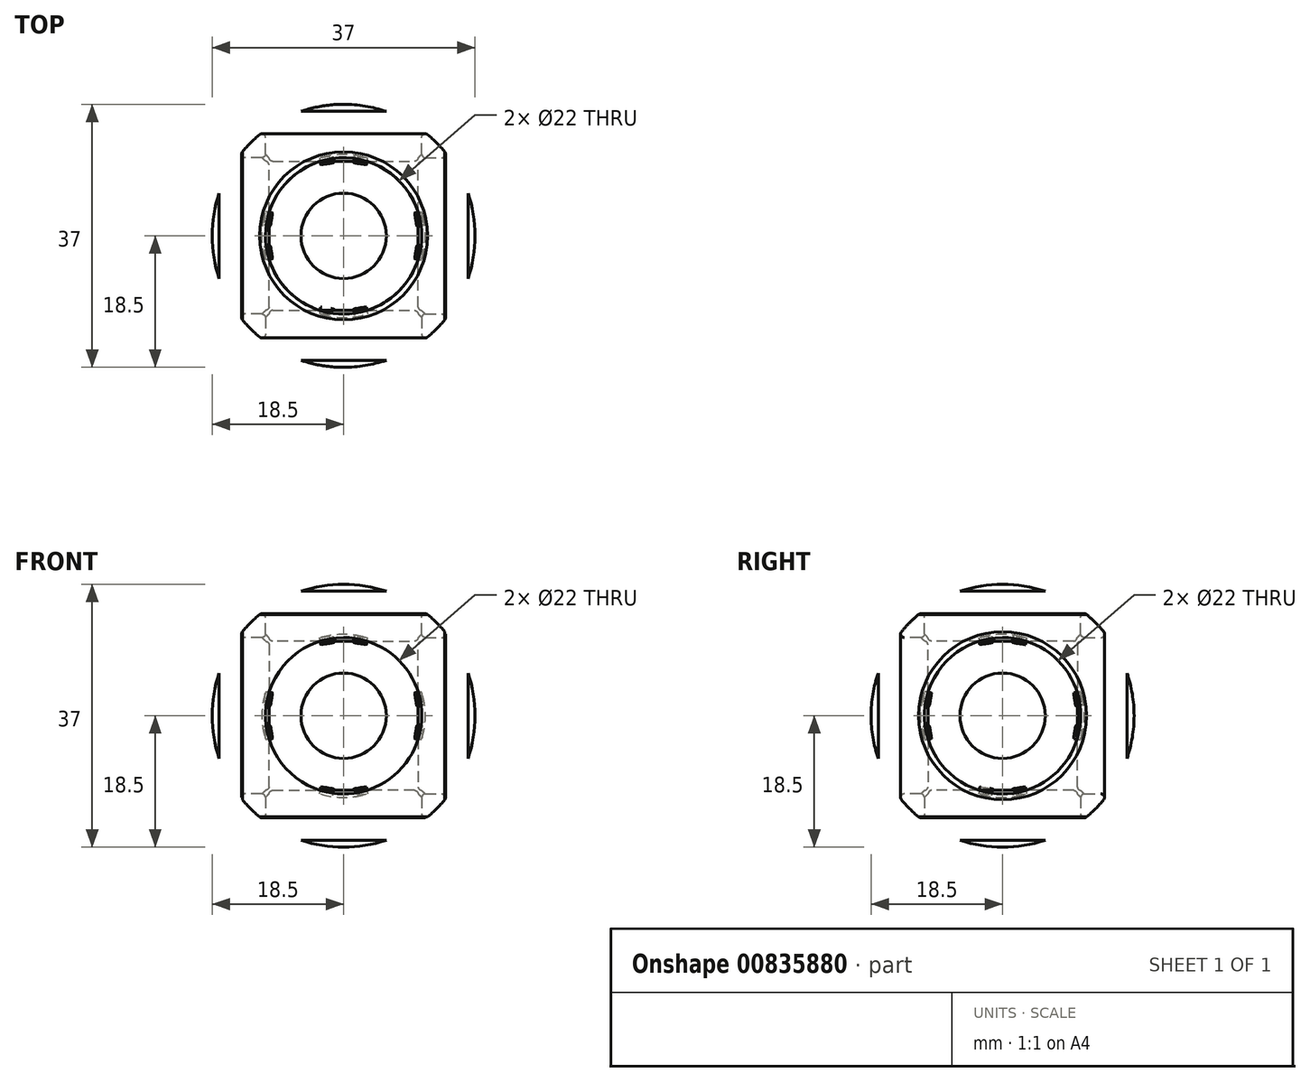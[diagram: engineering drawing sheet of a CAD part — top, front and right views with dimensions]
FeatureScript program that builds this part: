
annotation { "Feature Type Name" : "Feature", "Feature Type Description" : "" }
export const myFeature = defineFeature(function(context is Context, id is Id, definition is map)
    precondition{}
    {
        {
            var Q0;
            Q0=qCreatedBy(makeId("Top.planeOp"),FACE);
            var sketch = newSketch(context, id + "F0", { "sketchPlane" : qUnion([Q0])});
            skCircle(sketch, "E0", {"center": v(0, 0) * mm, "radius": 18.5 * mm});
            skLineSegment(sketch, "E1", {"start": v(0, 18.5) * mm, "end": v(0, -18.5) * mm});
            skSolve(sketch);
        }
        {
            var Q0;
            {var subQ0=sQuery(id+"F0.wireOp",EDGE,"E1");Q0=makeQuery(id+"F0.imprint","IMPRINT",FACE,{"disambiguationData":[TD([[makeQuery(id+"F0.imprint","IMPRINT",EDGE,{"derivedFrom":subQ0}),1.0]])]});}
            var Q1;
            Q1=sQuery(id+"F0.wireOp",EDGE,"E1");
            revolve(context, id + "F1", {"surfaceOperationType" : NewSurfaceOperationType.NEW, "entities" : qUnion([Q0]), "axis" : qUnion([Q1]), "revolveType" : RevolveType.FULL});
        }
        {
            var Q0;
            Q0=qCreatedBy(makeId("Right.planeOp"),FACE);
            cPlane(context, id + "F2", {"entities" : qUnion([Q0]), "cplaneType" : CPlaneType.OFFSET, "offset" : 17.5 * mm, "width" : 150 * mm, "height" : 150 * mm});
        }
        {
            var Q0;
            Q0=qCreatedBy(id+"F2.planeOp",FACE);
            var sketch = newSketch(context, id + "F3", { "sketchPlane" : qUnion([Q0])});
            skCircle(sketch, "E2", {"center": v(0, 0) * mm, "radius": 11 * mm});
            skSolve(sketch);
        }
        {
            var Q0;
            Q0 = qSketchRegion(id + "F3", true);
            extrude(context, id + "F4", {"entities" : qUnion([Q0]), "operationType" : NewBodyOperationType.REMOVE, "oppositeDirection" : true, "depth" : 7 * mm, "offsetDistance" : 25 * mm});
        }
        {
            var Q0;
            Q0=qCreatedBy(makeId("Front.planeOp"),FACE);
            cPlane(context, id + "F5", {"entities" : qUnion([Q0]), "cplaneType" : CPlaneType.OFFSET, "offset" : 17.5 * mm, "width" : 150 * mm, "height" : 150 * mm});
        }
        {
            var Q0;
            Q0=qCreatedBy(id+"F5.planeOp",FACE);
            var sketch = newSketch(context, id + "F6", { "sketchPlane" : qUnion([Q0])});
            skCircle(sketch, "E3", {"center": v(0, 0) * mm, "radius": 11 * mm});
            skSolve(sketch);
        }
        {
            var Q0;
            Q0 = qSketchRegion(id + "F6", true);
            extrude(context, id + "F7", {"entities" : qUnion([Q0]), "operationType" : NewBodyOperationType.REMOVE, "oppositeDirection" : true, "depth" : 7 * mm, "offsetDistance" : 25 * mm});
        }
        {
            var Q0;
            Q0=qCreatedBy(makeId("Front.planeOp"),FACE);
            cPlane(context, id + "F8", {"entities" : qUnion([Q0]), "cplaneType" : CPlaneType.OFFSET, "offset" : 17.5 * mm, "oppositeDirection" : true, "width" : 150 * mm, "height" : 150 * mm});
        }
        {
            var Q0;
            Q0=qCreatedBy(id+"F8.planeOp",FACE);
            var sketch = newSketch(context, id + "F9", { "sketchPlane" : qUnion([Q0])});
            skCircle(sketch, "E4", {"center": v(0, 0) * mm, "radius": 11 * mm});
            skSolve(sketch);
        }
        {
            var Q0;
            Q0 = qSketchRegion(id + "F9", true);
            extrude(context, id + "F10", {"entities" : qUnion([Q0]), "operationType" : NewBodyOperationType.REMOVE, "depth" : 7 * mm, "offsetDistance" : 25 * mm});
        }
        {
            var Q0;
            Q0=qCreatedBy(makeId("Right.planeOp"),FACE);
            cPlane(context, id + "F11", {"entities" : qUnion([Q0]), "cplaneType" : CPlaneType.OFFSET, "offset" : 17.5 * mm, "oppositeDirection" : true, "width" : 150 * mm, "height" : 150 * mm});
        }
        {
            var Q0;
            Q0=qCreatedBy(id+"F11.planeOp",FACE);
            var sketch = newSketch(context, id + "F12", { "sketchPlane" : qUnion([Q0])});
            skCircle(sketch, "E5", {"center": v(0, 0) * mm, "radius": 11 * mm});
            skSolve(sketch);
        }
        {
            var Q0;
            Q0 = qSketchRegion(id + "F12", true);
            extrude(context, id + "F13", {"entities" : qUnion([Q0]), "operationType" : NewBodyOperationType.REMOVE, "depth" : 7 * mm, "offsetDistance" : 25 * mm});
        }
        {
            var Q0;
            Q0=qCreatedBy(makeId("Top.planeOp"),FACE);
            cPlane(context, id + "F14", {"entities" : qUnion([Q0]), "cplaneType" : CPlaneType.OFFSET, "offset" : 17.5 * mm, "width" : 150 * mm, "height" : 150 * mm});
        }
        {
            var Q0;
            Q0=qCreatedBy(id+"F14.planeOp",FACE);
            var sketch = newSketch(context, id + "F15", { "sketchPlane" : qUnion([Q0])});
            skCircle(sketch, "E6", {"center": v(0, 0) * mm, "radius": 11 * mm});
            skSolve(sketch);
        }
        {
            var Q0;
            Q0 = qSketchRegion(id + "F15", true);
            extrude(context, id + "F16", {"entities" : qUnion([Q0]), "operationType" : NewBodyOperationType.REMOVE, "oppositeDirection" : true, "depth" : 7 * mm, "offsetDistance" : 25 * mm});
        }
        {
            var Q0;
            Q0=qCreatedBy(makeId("Top.planeOp"),FACE);
            cPlane(context, id + "F17", {"entities" : qUnion([Q0]), "cplaneType" : CPlaneType.OFFSET, "offset" : 17.5 * mm, "oppositeDirection" : true, "width" : 150 * mm, "height" : 150 * mm});
        }
        {
            var Q0;
            Q0=qCreatedBy(id+"F17.planeOp",FACE);
            var sketch = newSketch(context, id + "F18", { "sketchPlane" : qUnion([Q0])});
            skCircle(sketch, "E7", {"center": v(0, 0) * mm, "radius": 11 * mm});
            skSolve(sketch);
        }
        {
            var Q0;
            Q0 = qSketchRegion(id + "F18", true);
            extrude(context, id + "F19", {"entities" : qUnion([Q0]), "operationType" : NewBodyOperationType.REMOVE, "depth" : 7 * mm, "offsetDistance" : 25 * mm});
        }
        {
            var Q0;
            Q0=makeQuery(id+"F16.boolean.opBoolean","COPY",FACE,{"derivedFrom":makeQuery(id+"F16.opExtrude","SWEPT_FACE",FACE,{"disambiguationData":[OSD([sQuery(id+"F15.wireOp",EDGE,"E6")])]})});
            var Q1;
            Q1=makeQuery(id+"F16.boolean.opBoolean","INTERSECT",EDGE,{"derivedFrom":[makeQuery(id+"F1.opRevolve","SWEPT_FACE",FACE,{"disambiguationData":[OSD([sQuery(id+"F0.wireOp",EDGE,"E0")])]}),makeQuery(id+"F16.opExtrude","SWEPT_FACE",FACE,{"disambiguationData":[OSD([sQuery(id+"F15.wireOp",EDGE,"E6")])]})]});
            var Q2;
            Q2=makeQuery(id+"F16.boolean.opBoolean","COPY",FACE,{"derivedFrom":makeQuery(id+"F16.opExtrude","CAP_FACE",FACE,{"disambiguationData":[OSD([sQuery(id+"F15.wireOp",EDGE,"E6")])],"isStart":false})});
            var Q3;
            Q3=makeQuery(id+"F16.boolean.opBoolean","INTERSECT",EDGE,{"derivedFrom":[makeQuery(id+"F10.boolean.opBoolean","COPY",FACE,{"derivedFrom":makeQuery(id+"F10.opExtrude","SWEPT_FACE",FACE,{"disambiguationData":[OSD([sQuery(id+"F9.wireOp",EDGE,"E4")])]})}),makeQuery(id+"F16.opExtrude","SWEPT_FACE",FACE,{"disambiguationData":[OSD([sQuery(id+"F15.wireOp",EDGE,"E6")])]})]});
            var Q4;
            Q4=makeQuery(id+"F13.boolean.opBoolean","COPY",FACE,{"derivedFrom":makeQuery(id+"F13.opExtrude","SWEPT_FACE",FACE,{"disambiguationData":[OSD([sQuery(id+"F12.wireOp",EDGE,"E5")])]})});
            var Q5;
            Q5=makeQuery(id+"F10.boolean.opBoolean","COPY",FACE,{"derivedFrom":makeQuery(id+"F10.opExtrude","SWEPT_FACE",FACE,{"disambiguationData":[OSD([sQuery(id+"F9.wireOp",EDGE,"E4")])]})});
            var Q6;
            Q6=makeQuery(id+"F1.opRevolve","SWEPT_FACE",FACE,{"disambiguationData":[OSD([sQuery(id+"F0.wireOp",EDGE,"E0")])]});
            var Q7;
            Q7=makeQuery(id+"F4.boolean.opBoolean","INTERSECT",EDGE,{"derivedFrom":[makeQuery(id+"F1.opRevolve","SWEPT_FACE",FACE,{"disambiguationData":[OSD([sQuery(id+"F0.wireOp",EDGE,"E0")])]}),makeQuery(id+"F4.opExtrude","SWEPT_FACE",FACE,{"disambiguationData":[OSD([sQuery(id+"F3.wireOp",EDGE,"E2")])]})]});
            var Q8;
            Q8=makeQuery(id+"F13.boolean.opBoolean","INTERSECT",EDGE,{"derivedFrom":[makeQuery(id+"F1.opRevolve","SWEPT_FACE",FACE,{"disambiguationData":[OSD([sQuery(id+"F0.wireOp",EDGE,"E0")])]}),makeQuery(id+"F13.opExtrude","SWEPT_FACE",FACE,{"disambiguationData":[OSD([sQuery(id+"F12.wireOp",EDGE,"E5")])]})]});
            var Q9;
            Q9=makeQuery(id+"F7.boolean.opBoolean","INTERSECT",EDGE,{"derivedFrom":[makeQuery(id+"F1.opRevolve","SWEPT_FACE",FACE,{"disambiguationData":[OSD([sQuery(id+"F0.wireOp",EDGE,"E0")])]}),makeQuery(id+"F7.opExtrude","SWEPT_FACE",FACE,{"disambiguationData":[OSD([sQuery(id+"F6.wireOp",EDGE,"E3")])]})]});
            var Q10;
            Q10=makeQuery(id+"F10.boolean.opBoolean","INTERSECT",EDGE,{"derivedFrom":[makeQuery(id+"F1.opRevolve","SWEPT_FACE",FACE,{"disambiguationData":[OSD([sQuery(id+"F0.wireOp",EDGE,"E0")])]}),makeQuery(id+"F10.opExtrude","SWEPT_FACE",FACE,{"disambiguationData":[OSD([sQuery(id+"F9.wireOp",EDGE,"E4")])]})]});
            var Q11;
            Q11=makeQuery(id+"F16.boolean.opBoolean","INTERSECT",EDGE,{"derivedFrom":[makeQuery(id+"F4.boolean.opBoolean","COPY",FACE,{"derivedFrom":makeQuery(id+"F4.opExtrude","SWEPT_FACE",FACE,{"disambiguationData":[OSD([sQuery(id+"F3.wireOp",EDGE,"E2")])]})}),makeQuery(id+"F16.opExtrude","SWEPT_FACE",FACE,{"disambiguationData":[OSD([sQuery(id+"F15.wireOp",EDGE,"E6")])]})]});
            var Q12;
            {var subQ0=sQuery(id+"F12.wireOp",EDGE,"E5");var subQ1=sQuery(id+"F6.wireOp",EDGE,"E3");Q12=makeQuery(id+"F16.boolean.opBoolean","SPLIT",EDGE,{"disambiguationData":[TD([makeQuery(id+"F7.boolean.opBoolean","COPY",FACE,{"derivedFrom":makeQuery(id+"F7.opExtrude","SWEPT_FACE",FACE,{"disambiguationData":[OSD([subQ1])]})})])],"derivedFrom":makeQuery(id+"F13.boolean.opBoolean","COPY",EDGE,{"disambiguationData":[OD(1.0)],"derivedFrom":makeQuery(id+"F13.opExtrude","CAP_EDGE",EDGE,{"disambiguationData":[OSD([subQ0])],"isStart":false})})});}
            var Q13;
            {var subQ0=sQuery(id+"F12.wireOp",EDGE,"E5");var subQ1=sQuery(id+"F9.wireOp",EDGE,"E4");Q13=makeQuery(id+"F16.boolean.opBoolean","SPLIT",EDGE,{"disambiguationData":[TD([makeQuery(id+"F13.boolean.opBoolean","COPY",FACE,{"derivedFrom":makeQuery(id+"F13.opExtrude","SWEPT_FACE",FACE,{"disambiguationData":[OSD([subQ0])]})})])],"derivedFrom":makeQuery(id+"F13.boolean.opBoolean","SPLIT",EDGE,{"disambiguationData":[OD(1.0)],"derivedFrom":makeQuery(id+"F10.boolean.opBoolean","COPY",EDGE,{"derivedFrom":makeQuery(id+"F10.opExtrude","CAP_EDGE",EDGE,{"disambiguationData":[OSD([subQ1])],"isStart":false})})})});}
            var Q14;
            {var subQ0=sQuery(id+"F9.wireOp",EDGE,"E4");var subQ1=sQuery(id+"F3.wireOp",EDGE,"E2");Q14=makeQuery(id+"F16.boolean.opBoolean","SPLIT",EDGE,{"disambiguationData":[TD([makeQuery(id+"F4.boolean.opBoolean","COPY",FACE,{"derivedFrom":makeQuery(id+"F4.opExtrude","SWEPT_FACE",FACE,{"disambiguationData":[OSD([subQ1])]})})])],"derivedFrom":makeQuery(id+"F13.boolean.opBoolean","SPLIT",EDGE,{"disambiguationData":[OD(1.0)],"derivedFrom":makeQuery(id+"F10.boolean.opBoolean","COPY",EDGE,{"derivedFrom":makeQuery(id+"F10.opExtrude","CAP_EDGE",EDGE,{"disambiguationData":[OSD([subQ0])],"isStart":false})})})});}
            var Q15;
            Q15=makeQuery(id+"F16.boolean.opBoolean","INTERSECT",EDGE,{"derivedFrom":[makeQuery(id+"F13.boolean.opBoolean","COPY",FACE,{"derivedFrom":makeQuery(id+"F13.opExtrude","SWEPT_FACE",FACE,{"disambiguationData":[OSD([sQuery(id+"F12.wireOp",EDGE,"E5")])]})}),makeQuery(id+"F16.opExtrude","SWEPT_FACE",FACE,{"disambiguationData":[OSD([sQuery(id+"F15.wireOp",EDGE,"E6")])]})]});
            var Q16;
            Q16=makeQuery(id+"F4.boolean.opBoolean","COPY",FACE,{"derivedFrom":makeQuery(id+"F4.opExtrude","SWEPT_FACE",FACE,{"disambiguationData":[OSD([sQuery(id+"F3.wireOp",EDGE,"E2")])]})});
            var Q17;
            Q17=makeQuery(id+"F16.boolean.opBoolean","INTERSECT",EDGE,{"derivedFrom":[makeQuery(id+"F7.boolean.opBoolean","COPY",FACE,{"derivedFrom":makeQuery(id+"F7.opExtrude","SWEPT_FACE",FACE,{"disambiguationData":[OSD([sQuery(id+"F6.wireOp",EDGE,"E3")])]})}),makeQuery(id+"F16.opExtrude","SWEPT_FACE",FACE,{"disambiguationData":[OSD([sQuery(id+"F15.wireOp",EDGE,"E6")])]})]});
            var Q18;
            Q18=makeQuery(id+"F19.boolean.opBoolean","COPY",FACE,{"derivedFrom":makeQuery(id+"F19.opExtrude","CAP_FACE",FACE,{"disambiguationData":[OSD([sQuery(id+"F18.wireOp",EDGE,"E7")])],"isStart":false})});
            var Q19;
            Q19=makeQuery(id+"F16.boolean.opBoolean","INTERSECT",EDGE,{"derivedFrom":[makeQuery(id+"F13.boolean.opBoolean","COPY",FACE,{"derivedFrom":makeQuery(id+"F13.opExtrude","CAP_FACE",FACE,{"disambiguationData":[OSD([sQuery(id+"F12.wireOp",EDGE,"E5")])],"isStart":false})}),makeQuery(id+"F16.opExtrude","CAP_FACE",FACE,{"disambiguationData":[OSD([sQuery(id+"F15.wireOp",EDGE,"E6")])],"isStart":false})]});
            var Q20;
            Q20=makeQuery(id+"F16.boolean.opBoolean","INTERSECT",EDGE,{"derivedFrom":[makeQuery(id+"F10.boolean.opBoolean","COPY",FACE,{"derivedFrom":makeQuery(id+"F10.opExtrude","CAP_FACE",FACE,{"disambiguationData":[OSD([sQuery(id+"F9.wireOp",EDGE,"E4")])],"isStart":false})}),makeQuery(id+"F16.opExtrude","CAP_FACE",FACE,{"disambiguationData":[OSD([sQuery(id+"F15.wireOp",EDGE,"E6")])],"isStart":false})]});
            var Q21;
            {var subQ0=sQuery(id+"F6.wireOp",EDGE,"E3");var subQ2=sQuery(id+"F3.wireOp",EDGE,"E2");Q21=makeQuery(id+"F16.boolean.opBoolean","SPLIT",EDGE,{"disambiguationData":[TD([makeQuery(id+"F7.boolean.opBoolean","COPY",FACE,{"derivedFrom":makeQuery(id+"F7.opExtrude","SWEPT_FACE",FACE,{"disambiguationData":[OSD([subQ0])]})})])],"derivedFrom":makeQuery(id+"F10.boolean.opBoolean","SPLIT",EDGE,{"disambiguationData":[OD(1.0)],"derivedFrom":makeQuery(id+"F4.boolean.opBoolean","COPY",EDGE,{"derivedFrom":makeQuery(id+"F4.opExtrude","CAP_EDGE",EDGE,{"disambiguationData":[OSD([subQ2])],"isStart":false})})})});}
            var Q22;
            {var subQ0=sQuery(id+"F9.wireOp",EDGE,"E4");var subQ1=sQuery(id+"F3.wireOp",EDGE,"E2");Q22=makeQuery(id+"F16.boolean.opBoolean","SPLIT",EDGE,{"disambiguationData":[TD([makeQuery(id+"F10.boolean.opBoolean","COPY",FACE,{"derivedFrom":makeQuery(id+"F10.opExtrude","SWEPT_FACE",FACE,{"disambiguationData":[OSD([subQ0])]})})])],"derivedFrom":makeQuery(id+"F10.boolean.opBoolean","SPLIT",EDGE,{"disambiguationData":[OD(1.0)],"derivedFrom":makeQuery(id+"F4.boolean.opBoolean","COPY",EDGE,{"derivedFrom":makeQuery(id+"F4.opExtrude","CAP_EDGE",EDGE,{"disambiguationData":[OSD([subQ1])],"isStart":false})})})});}
            var Q23;
            {var subQ0=sQuery(id+"F6.wireOp",EDGE,"E3");var subQ2=sQuery(id+"F3.wireOp",EDGE,"E2");Q23=makeQuery(id+"F16.boolean.opBoolean","SPLIT",EDGE,{"disambiguationData":[TD([makeQuery(id+"F4.boolean.opBoolean","COPY",FACE,{"derivedFrom":makeQuery(id+"F4.opExtrude","SWEPT_FACE",FACE,{"disambiguationData":[OSD([subQ2])]})})])],"derivedFrom":makeQuery(id+"F13.boolean.opBoolean","SPLIT",EDGE,{"disambiguationData":[OD(1.0)],"derivedFrom":makeQuery(id+"F7.boolean.opBoolean","COPY",EDGE,{"derivedFrom":makeQuery(id+"F7.opExtrude","CAP_EDGE",EDGE,{"disambiguationData":[OSD([subQ0])],"isStart":false})})})});}
            var Q24;
            {var subQ0=sQuery(id+"F12.wireOp",EDGE,"E5");var subQ1=sQuery(id+"F6.wireOp",EDGE,"E3");Q24=makeQuery(id+"F16.boolean.opBoolean","SPLIT",EDGE,{"disambiguationData":[TD([makeQuery(id+"F13.boolean.opBoolean","COPY",FACE,{"derivedFrom":makeQuery(id+"F13.opExtrude","SWEPT_FACE",FACE,{"disambiguationData":[OSD([subQ0])]})})])],"derivedFrom":makeQuery(id+"F13.boolean.opBoolean","SPLIT",EDGE,{"disambiguationData":[OD(1.0)],"derivedFrom":makeQuery(id+"F7.boolean.opBoolean","COPY",EDGE,{"derivedFrom":makeQuery(id+"F7.opExtrude","CAP_EDGE",EDGE,{"disambiguationData":[OSD([subQ1])],"isStart":false})})})});}
            var Q25;
            {var subQ0=sQuery(id+"F12.wireOp",EDGE,"E5");var subQ1=sQuery(id+"F9.wireOp",EDGE,"E4");Q25=makeQuery(id+"F16.boolean.opBoolean","SPLIT",EDGE,{"disambiguationData":[TD([makeQuery(id+"F10.boolean.opBoolean","COPY",FACE,{"derivedFrom":makeQuery(id+"F10.opExtrude","SWEPT_FACE",FACE,{"disambiguationData":[OSD([subQ1])]})})])],"derivedFrom":makeQuery(id+"F13.boolean.opBoolean","COPY",EDGE,{"disambiguationData":[OD(1.0)],"derivedFrom":makeQuery(id+"F13.opExtrude","CAP_EDGE",EDGE,{"disambiguationData":[OSD([subQ0])],"isStart":false})})});}
            var Q26;
            {var subQ0=sQuery(id+"F6.wireOp",EDGE,"E3");var subQ1=sQuery(id+"F15.wireOp",EDGE,"E6");var subQ2=sQuery(id+"F3.wireOp",EDGE,"E2");Q26=makeQuery(id+"F16.boolean.opBoolean","COPY",EDGE,{"disambiguationData":[TD([makeQuery(id+"F4.boolean.opBoolean","COPY",FACE,{"derivedFrom":makeQuery(id+"F4.opExtrude","SWEPT_FACE",FACE,{"disambiguationData":[OSD([subQ2])]})}),makeQuery(id+"F4.boolean.opBoolean","COPY",FACE,{"derivedFrom":makeQuery(id+"F4.opExtrude","CAP_FACE",FACE,{"disambiguationData":[OSD([subQ2])],"isStart":false})}),makeQuery(id+"F7.boolean.opBoolean","COPY",FACE,{"derivedFrom":makeQuery(id+"F7.opExtrude","SWEPT_FACE",FACE,{"disambiguationData":[OSD([subQ0])]})}),makeQuery(id+"F7.boolean.opBoolean","COPY",FACE,{"derivedFrom":makeQuery(id+"F7.opExtrude","CAP_FACE",FACE,{"disambiguationData":[OSD([subQ0])],"isStart":false})}),makeQuery(id+"F16.opExtrude","SWEPT_FACE",FACE,{"disambiguationData":[OSD([subQ1])]}),makeQuery(id+"F16.opExtrude","CAP_FACE",FACE,{"disambiguationData":[OSD([subQ1])],"isStart":false})])],"derivedFrom":makeQuery(id+"F16.opExtrude","CAP_EDGE",EDGE,{"disambiguationData":[OSD([subQ1])],"isStart":false})});}
            var Q27;
            {var subQ0=sQuery(id+"F9.wireOp",EDGE,"E4");var subQ1=sQuery(id+"F3.wireOp",EDGE,"E2");var subQ2=sQuery(id+"F15.wireOp",EDGE,"E6");Q27=makeQuery(id+"F16.boolean.opBoolean","COPY",EDGE,{"disambiguationData":[TD([makeQuery(id+"F4.boolean.opBoolean","COPY",FACE,{"derivedFrom":makeQuery(id+"F4.opExtrude","SWEPT_FACE",FACE,{"disambiguationData":[OSD([subQ1])]})}),makeQuery(id+"F4.boolean.opBoolean","COPY",FACE,{"derivedFrom":makeQuery(id+"F4.opExtrude","CAP_FACE",FACE,{"disambiguationData":[OSD([subQ1])],"isStart":false})}),makeQuery(id+"F10.boolean.opBoolean","COPY",FACE,{"derivedFrom":makeQuery(id+"F10.opExtrude","SWEPT_FACE",FACE,{"disambiguationData":[OSD([subQ0])]})}),makeQuery(id+"F10.boolean.opBoolean","COPY",FACE,{"derivedFrom":makeQuery(id+"F10.opExtrude","CAP_FACE",FACE,{"disambiguationData":[OSD([subQ0])],"isStart":false})}),makeQuery(id+"F16.opExtrude","SWEPT_FACE",FACE,{"disambiguationData":[OSD([subQ2])]}),makeQuery(id+"F16.opExtrude","CAP_FACE",FACE,{"disambiguationData":[OSD([subQ2])],"isStart":false})])],"derivedFrom":makeQuery(id+"F16.opExtrude","CAP_EDGE",EDGE,{"disambiguationData":[OSD([subQ2])],"isStart":false})});}
            var Q28;
            {var subQ0=sQuery(id+"F12.wireOp",EDGE,"E5");var subQ1=sQuery(id+"F6.wireOp",EDGE,"E3");var subQ2=sQuery(id+"F15.wireOp",EDGE,"E6");Q28=makeQuery(id+"F16.boolean.opBoolean","COPY",EDGE,{"disambiguationData":[TD([makeQuery(id+"F7.boolean.opBoolean","COPY",FACE,{"derivedFrom":makeQuery(id+"F7.opExtrude","SWEPT_FACE",FACE,{"disambiguationData":[OSD([subQ1])]})}),makeQuery(id+"F7.boolean.opBoolean","COPY",FACE,{"derivedFrom":makeQuery(id+"F7.opExtrude","CAP_FACE",FACE,{"disambiguationData":[OSD([subQ1])],"isStart":false})}),makeQuery(id+"F13.boolean.opBoolean","COPY",FACE,{"derivedFrom":makeQuery(id+"F13.opExtrude","SWEPT_FACE",FACE,{"disambiguationData":[OSD([subQ0])]})}),makeQuery(id+"F13.boolean.opBoolean","COPY",FACE,{"derivedFrom":makeQuery(id+"F13.opExtrude","CAP_FACE",FACE,{"disambiguationData":[OSD([subQ0])],"isStart":false})}),makeQuery(id+"F16.opExtrude","SWEPT_FACE",FACE,{"disambiguationData":[OSD([subQ2])]}),makeQuery(id+"F16.opExtrude","CAP_FACE",FACE,{"disambiguationData":[OSD([subQ2])],"isStart":false})])],"derivedFrom":makeQuery(id+"F16.opExtrude","CAP_EDGE",EDGE,{"disambiguationData":[OSD([subQ2])],"isStart":false})});}
            var Q29;
            {var subQ0=sQuery(id+"F12.wireOp",EDGE,"E5");var subQ1=sQuery(id+"F9.wireOp",EDGE,"E4");var subQ2=sQuery(id+"F15.wireOp",EDGE,"E6");Q29=makeQuery(id+"F16.boolean.opBoolean","COPY",EDGE,{"disambiguationData":[TD([makeQuery(id+"F10.boolean.opBoolean","COPY",FACE,{"derivedFrom":makeQuery(id+"F10.opExtrude","SWEPT_FACE",FACE,{"disambiguationData":[OSD([subQ1])]})}),makeQuery(id+"F10.boolean.opBoolean","COPY",FACE,{"derivedFrom":makeQuery(id+"F10.opExtrude","CAP_FACE",FACE,{"disambiguationData":[OSD([subQ1])],"isStart":false})}),makeQuery(id+"F13.boolean.opBoolean","COPY",FACE,{"derivedFrom":makeQuery(id+"F13.opExtrude","SWEPT_FACE",FACE,{"disambiguationData":[OSD([subQ0])]})}),makeQuery(id+"F13.boolean.opBoolean","COPY",FACE,{"derivedFrom":makeQuery(id+"F13.opExtrude","CAP_FACE",FACE,{"disambiguationData":[OSD([subQ0])],"isStart":false})}),makeQuery(id+"F16.opExtrude","SWEPT_FACE",FACE,{"disambiguationData":[OSD([subQ2])]}),makeQuery(id+"F16.opExtrude","CAP_FACE",FACE,{"disambiguationData":[OSD([subQ2])],"isStart":false})])],"derivedFrom":makeQuery(id+"F16.opExtrude","CAP_EDGE",EDGE,{"disambiguationData":[OSD([subQ2])],"isStart":false})});}
            var Q30;
            Q30=makeQuery(id+"F4.boolean.opBoolean","COPY",FACE,{"derivedFrom":makeQuery(id+"F4.opExtrude","CAP_FACE",FACE,{"disambiguationData":[OSD([sQuery(id+"F3.wireOp",EDGE,"E2")])],"isStart":false})});
            var Q31;
            Q31=makeQuery(id+"F19.boolean.opBoolean","INTERSECT",EDGE,{"derivedFrom":[makeQuery(id+"F10.boolean.opBoolean","COPY",FACE,{"derivedFrom":makeQuery(id+"F10.opExtrude","SWEPT_FACE",FACE,{"disambiguationData":[OSD([sQuery(id+"F9.wireOp",EDGE,"E4")])]})}),makeQuery(id+"F19.opExtrude","SWEPT_FACE",FACE,{"disambiguationData":[OSD([sQuery(id+"F18.wireOp",EDGE,"E7")])]})]});
            var Q32;
            Q32=makeQuery(id+"F13.boolean.opBoolean","COPY",FACE,{"derivedFrom":makeQuery(id+"F13.opExtrude","CAP_FACE",FACE,{"disambiguationData":[OSD([sQuery(id+"F12.wireOp",EDGE,"E5")])],"isStart":false})});
            var Q33;
            Q33=makeQuery(id+"F7.boolean.opBoolean","COPY",FACE,{"derivedFrom":makeQuery(id+"F7.opExtrude","SWEPT_FACE",FACE,{"disambiguationData":[OSD([sQuery(id+"F6.wireOp",EDGE,"E3")])]})});
            var Q34;
            Q34=makeQuery(id+"F7.boolean.opBoolean","COPY",FACE,{"derivedFrom":makeQuery(id+"F7.opExtrude","CAP_FACE",FACE,{"disambiguationData":[OSD([sQuery(id+"F6.wireOp",EDGE,"E3")])],"isStart":false})});
            var Q35;
            Q35=makeQuery(id+"F10.boolean.opBoolean","COPY",FACE,{"derivedFrom":makeQuery(id+"F10.opExtrude","CAP_FACE",FACE,{"disambiguationData":[OSD([sQuery(id+"F9.wireOp",EDGE,"E4")])],"isStart":false})});
            var Q36;
            Q36=makeQuery(id+"F7.boolean.opBoolean","INTERSECT",EDGE,{"derivedFrom":[makeQuery(id+"F4.boolean.opBoolean","COPY",FACE,{"derivedFrom":makeQuery(id+"F4.opExtrude","SWEPT_FACE",FACE,{"disambiguationData":[OSD([sQuery(id+"F3.wireOp",EDGE,"E2")])]})}),makeQuery(id+"F7.opExtrude","SWEPT_FACE",FACE,{"disambiguationData":[OSD([sQuery(id+"F6.wireOp",EDGE,"E3")])]})]});
            var Q37;
            Q37=makeQuery(id+"F7.boolean.opBoolean","INTERSECT",EDGE,{"derivedFrom":[makeQuery(id+"F4.boolean.opBoolean","COPY",FACE,{"derivedFrom":makeQuery(id+"F4.opExtrude","CAP_FACE",FACE,{"disambiguationData":[OSD([sQuery(id+"F3.wireOp",EDGE,"E2")])],"isStart":false})}),makeQuery(id+"F7.opExtrude","CAP_FACE",FACE,{"disambiguationData":[OSD([sQuery(id+"F6.wireOp",EDGE,"E3")])],"isStart":false})]});
            var Q38;
            Q38=makeQuery(id+"F13.boolean.opBoolean","INTERSECT",EDGE,{"derivedFrom":[makeQuery(id+"F7.boolean.opBoolean","COPY",FACE,{"derivedFrom":makeQuery(id+"F7.opExtrude","SWEPT_FACE",FACE,{"disambiguationData":[OSD([sQuery(id+"F6.wireOp",EDGE,"E3")])]})}),makeQuery(id+"F13.opExtrude","SWEPT_FACE",FACE,{"disambiguationData":[OSD([sQuery(id+"F12.wireOp",EDGE,"E5")])]})]});
            var Q39;
            Q39=makeQuery(id+"F10.boolean.opBoolean","INTERSECT",EDGE,{"derivedFrom":[makeQuery(id+"F4.boolean.opBoolean","COPY",FACE,{"derivedFrom":makeQuery(id+"F4.opExtrude","SWEPT_FACE",FACE,{"disambiguationData":[OSD([sQuery(id+"F3.wireOp",EDGE,"E2")])]})}),makeQuery(id+"F10.opExtrude","SWEPT_FACE",FACE,{"disambiguationData":[OSD([sQuery(id+"F9.wireOp",EDGE,"E4")])]})]});
            var Q40;
            Q40=makeQuery(id+"F10.boolean.opBoolean","INTERSECT",EDGE,{"derivedFrom":[makeQuery(id+"F4.boolean.opBoolean","COPY",FACE,{"derivedFrom":makeQuery(id+"F4.opExtrude","CAP_FACE",FACE,{"disambiguationData":[OSD([sQuery(id+"F3.wireOp",EDGE,"E2")])],"isStart":false})}),makeQuery(id+"F10.opExtrude","CAP_FACE",FACE,{"disambiguationData":[OSD([sQuery(id+"F9.wireOp",EDGE,"E4")])],"isStart":false})]});
            var Q41;
            Q41=makeQuery(id+"F13.boolean.opBoolean","INTERSECT",EDGE,{"derivedFrom":[makeQuery(id+"F10.boolean.opBoolean","COPY",FACE,{"derivedFrom":makeQuery(id+"F10.opExtrude","SWEPT_FACE",FACE,{"disambiguationData":[OSD([sQuery(id+"F9.wireOp",EDGE,"E4")])]})}),makeQuery(id+"F13.opExtrude","SWEPT_FACE",FACE,{"disambiguationData":[OSD([sQuery(id+"F12.wireOp",EDGE,"E5")])]})]});
            var Q42;
            Q42=makeQuery(id+"F13.boolean.opBoolean","INTERSECT",EDGE,{"derivedFrom":[makeQuery(id+"F7.boolean.opBoolean","COPY",FACE,{"derivedFrom":makeQuery(id+"F7.opExtrude","CAP_FACE",FACE,{"disambiguationData":[OSD([sQuery(id+"F6.wireOp",EDGE,"E3")])],"isStart":false})}),makeQuery(id+"F13.opExtrude","CAP_FACE",FACE,{"disambiguationData":[OSD([sQuery(id+"F12.wireOp",EDGE,"E5")])],"isStart":false})]});
            var Q43;
            Q43=makeQuery(id+"F13.boolean.opBoolean","INTERSECT",EDGE,{"derivedFrom":[makeQuery(id+"F10.boolean.opBoolean","COPY",FACE,{"derivedFrom":makeQuery(id+"F10.opExtrude","CAP_FACE",FACE,{"disambiguationData":[OSD([sQuery(id+"F9.wireOp",EDGE,"E4")])],"isStart":false})}),makeQuery(id+"F13.opExtrude","CAP_FACE",FACE,{"disambiguationData":[OSD([sQuery(id+"F12.wireOp",EDGE,"E5")])],"isStart":false})]});
            var Q44;
            Q44=makeQuery(id+"F19.boolean.opBoolean","INTERSECT",EDGE,{"derivedFrom":[makeQuery(id+"F13.boolean.opBoolean","COPY",FACE,{"derivedFrom":makeQuery(id+"F13.opExtrude","SWEPT_FACE",FACE,{"disambiguationData":[OSD([sQuery(id+"F12.wireOp",EDGE,"E5")])]})}),makeQuery(id+"F19.opExtrude","SWEPT_FACE",FACE,{"disambiguationData":[OSD([sQuery(id+"F18.wireOp",EDGE,"E7")])]})]});
            var Q45;
            Q45=makeQuery(id+"F16.boolean.opBoolean","INTERSECT",EDGE,{"derivedFrom":[makeQuery(id+"F4.boolean.opBoolean","COPY",FACE,{"derivedFrom":makeQuery(id+"F4.opExtrude","CAP_FACE",FACE,{"disambiguationData":[OSD([sQuery(id+"F3.wireOp",EDGE,"E2")])],"isStart":false})}),makeQuery(id+"F16.opExtrude","CAP_FACE",FACE,{"disambiguationData":[OSD([sQuery(id+"F15.wireOp",EDGE,"E6")])],"isStart":false})]});
            var Q46;
            Q46=makeQuery(id+"F19.boolean.opBoolean","INTERSECT",EDGE,{"derivedFrom":[makeQuery(id+"F4.boolean.opBoolean","COPY",FACE,{"derivedFrom":makeQuery(id+"F4.opExtrude","SWEPT_FACE",FACE,{"disambiguationData":[OSD([sQuery(id+"F3.wireOp",EDGE,"E2")])]})}),makeQuery(id+"F19.opExtrude","SWEPT_FACE",FACE,{"disambiguationData":[OSD([sQuery(id+"F18.wireOp",EDGE,"E7")])]})]});
            var Q47;
            Q47=makeQuery(id+"F19.boolean.opBoolean","COPY",FACE,{"derivedFrom":makeQuery(id+"F19.opExtrude","SWEPT_FACE",FACE,{"disambiguationData":[OSD([sQuery(id+"F18.wireOp",EDGE,"E7")])]})});
            var Q48;
            Q48=makeQuery(id+"F16.boolean.opBoolean","INTERSECT",EDGE,{"derivedFrom":[makeQuery(id+"F7.boolean.opBoolean","COPY",FACE,{"derivedFrom":makeQuery(id+"F7.opExtrude","CAP_FACE",FACE,{"disambiguationData":[OSD([sQuery(id+"F6.wireOp",EDGE,"E3")])],"isStart":false})}),makeQuery(id+"F16.opExtrude","CAP_FACE",FACE,{"disambiguationData":[OSD([sQuery(id+"F15.wireOp",EDGE,"E6")])],"isStart":false})]});
            var Q49;
            {var subQ0=sQuery(id+"F12.wireOp",EDGE,"E5");var subQ1=sQuery(id+"F6.wireOp",EDGE,"E3");Q49=makeQuery(id+"F19.boolean.opBoolean","SPLIT",EDGE,{"disambiguationData":[TD([makeQuery(id+"F7.boolean.opBoolean","COPY",FACE,{"derivedFrom":makeQuery(id+"F7.opExtrude","SWEPT_FACE",FACE,{"disambiguationData":[OSD([subQ1])]})})])],"derivedFrom":makeQuery(id+"F13.boolean.opBoolean","COPY",EDGE,{"disambiguationData":[OD(0.0)],"derivedFrom":makeQuery(id+"F13.opExtrude","CAP_EDGE",EDGE,{"disambiguationData":[OSD([subQ0])],"isStart":false})})});}
            var Q50;
            {var subQ0=sQuery(id+"F12.wireOp",EDGE,"E5");var subQ1=sQuery(id+"F9.wireOp",EDGE,"E4");Q50=makeQuery(id+"F19.boolean.opBoolean","SPLIT",EDGE,{"disambiguationData":[TD([makeQuery(id+"F13.boolean.opBoolean","COPY",FACE,{"derivedFrom":makeQuery(id+"F13.opExtrude","SWEPT_FACE",FACE,{"disambiguationData":[OSD([subQ0])]})})])],"derivedFrom":makeQuery(id+"F13.boolean.opBoolean","SPLIT",EDGE,{"disambiguationData":[OD(0.0)],"derivedFrom":makeQuery(id+"F10.boolean.opBoolean","COPY",EDGE,{"derivedFrom":makeQuery(id+"F10.opExtrude","CAP_EDGE",EDGE,{"disambiguationData":[OSD([subQ1])],"isStart":false})})})});}
            var Q51;
            {var subQ0=sQuery(id+"F9.wireOp",EDGE,"E4");var subQ2=sQuery(id+"F3.wireOp",EDGE,"E2");Q51=makeQuery(id+"F19.boolean.opBoolean","SPLIT",EDGE,{"disambiguationData":[TD([makeQuery(id+"F4.boolean.opBoolean","COPY",FACE,{"derivedFrom":makeQuery(id+"F4.opExtrude","SWEPT_FACE",FACE,{"disambiguationData":[OSD([subQ2])]})})])],"derivedFrom":makeQuery(id+"F13.boolean.opBoolean","SPLIT",EDGE,{"disambiguationData":[OD(0.0)],"derivedFrom":makeQuery(id+"F10.boolean.opBoolean","COPY",EDGE,{"derivedFrom":makeQuery(id+"F10.opExtrude","CAP_EDGE",EDGE,{"disambiguationData":[OSD([subQ0])],"isStart":false})})})});}
            var Q52;
            Q52=makeQuery(id+"F19.boolean.opBoolean","INTERSECT",EDGE,{"derivedFrom":[makeQuery(id+"F7.boolean.opBoolean","COPY",FACE,{"derivedFrom":makeQuery(id+"F7.opExtrude","SWEPT_FACE",FACE,{"disambiguationData":[OSD([sQuery(id+"F6.wireOp",EDGE,"E3")])]})}),makeQuery(id+"F19.opExtrude","SWEPT_FACE",FACE,{"disambiguationData":[OSD([sQuery(id+"F18.wireOp",EDGE,"E7")])]})]});
            var Q53;
            Q53=makeQuery(id+"F19.boolean.opBoolean","INTERSECT",EDGE,{"derivedFrom":[makeQuery(id+"F13.boolean.opBoolean","COPY",FACE,{"derivedFrom":makeQuery(id+"F13.opExtrude","CAP_FACE",FACE,{"disambiguationData":[OSD([sQuery(id+"F12.wireOp",EDGE,"E5")])],"isStart":false})}),makeQuery(id+"F19.opExtrude","CAP_FACE",FACE,{"disambiguationData":[OSD([sQuery(id+"F18.wireOp",EDGE,"E7")])],"isStart":false})]});
            var Q54;
            Q54=makeQuery(id+"F19.boolean.opBoolean","INTERSECT",EDGE,{"derivedFrom":[makeQuery(id+"F10.boolean.opBoolean","COPY",FACE,{"derivedFrom":makeQuery(id+"F10.opExtrude","CAP_FACE",FACE,{"disambiguationData":[OSD([sQuery(id+"F9.wireOp",EDGE,"E4")])],"isStart":false})}),makeQuery(id+"F19.opExtrude","CAP_FACE",FACE,{"disambiguationData":[OSD([sQuery(id+"F18.wireOp",EDGE,"E7")])],"isStart":false})]});
            var Q55;
            {var subQ0=sQuery(id+"F6.wireOp",EDGE,"E3");var subQ2=sQuery(id+"F3.wireOp",EDGE,"E2");Q55=makeQuery(id+"F19.boolean.opBoolean","SPLIT",EDGE,{"disambiguationData":[TD([makeQuery(id+"F7.boolean.opBoolean","COPY",FACE,{"derivedFrom":makeQuery(id+"F7.opExtrude","SWEPT_FACE",FACE,{"disambiguationData":[OSD([subQ0])]})})])],"derivedFrom":makeQuery(id+"F10.boolean.opBoolean","SPLIT",EDGE,{"disambiguationData":[OD(0.0)],"derivedFrom":makeQuery(id+"F4.boolean.opBoolean","COPY",EDGE,{"derivedFrom":makeQuery(id+"F4.opExtrude","CAP_EDGE",EDGE,{"disambiguationData":[OSD([subQ2])],"isStart":false})})})});}
            var Q56;
            {var subQ0=sQuery(id+"F9.wireOp",EDGE,"E4");var subQ2=sQuery(id+"F3.wireOp",EDGE,"E2");Q56=makeQuery(id+"F19.boolean.opBoolean","SPLIT",EDGE,{"disambiguationData":[TD([makeQuery(id+"F10.boolean.opBoolean","COPY",FACE,{"derivedFrom":makeQuery(id+"F10.opExtrude","SWEPT_FACE",FACE,{"disambiguationData":[OSD([subQ0])]})})])],"derivedFrom":makeQuery(id+"F10.boolean.opBoolean","SPLIT",EDGE,{"disambiguationData":[OD(0.0)],"derivedFrom":makeQuery(id+"F4.boolean.opBoolean","COPY",EDGE,{"derivedFrom":makeQuery(id+"F4.opExtrude","CAP_EDGE",EDGE,{"disambiguationData":[OSD([subQ2])],"isStart":false})})})});}
            var Q57;
            {var subQ0=sQuery(id+"F6.wireOp",EDGE,"E3");var subQ2=sQuery(id+"F3.wireOp",EDGE,"E2");Q57=makeQuery(id+"F19.boolean.opBoolean","SPLIT",EDGE,{"disambiguationData":[TD([makeQuery(id+"F4.boolean.opBoolean","COPY",FACE,{"derivedFrom":makeQuery(id+"F4.opExtrude","SWEPT_FACE",FACE,{"disambiguationData":[OSD([subQ2])]})})])],"derivedFrom":makeQuery(id+"F13.boolean.opBoolean","SPLIT",EDGE,{"disambiguationData":[OD(0.0)],"derivedFrom":makeQuery(id+"F7.boolean.opBoolean","COPY",EDGE,{"derivedFrom":makeQuery(id+"F7.opExtrude","CAP_EDGE",EDGE,{"disambiguationData":[OSD([subQ0])],"isStart":false})})})});}
            var Q58;
            {var subQ0=sQuery(id+"F12.wireOp",EDGE,"E5");var subQ1=sQuery(id+"F6.wireOp",EDGE,"E3");Q58=makeQuery(id+"F19.boolean.opBoolean","SPLIT",EDGE,{"disambiguationData":[TD([makeQuery(id+"F13.boolean.opBoolean","COPY",FACE,{"derivedFrom":makeQuery(id+"F13.opExtrude","SWEPT_FACE",FACE,{"disambiguationData":[OSD([subQ0])]})})])],"derivedFrom":makeQuery(id+"F13.boolean.opBoolean","SPLIT",EDGE,{"disambiguationData":[OD(0.0)],"derivedFrom":makeQuery(id+"F7.boolean.opBoolean","COPY",EDGE,{"derivedFrom":makeQuery(id+"F7.opExtrude","CAP_EDGE",EDGE,{"disambiguationData":[OSD([subQ1])],"isStart":false})})})});}
            var Q59;
            {var subQ0=sQuery(id+"F12.wireOp",EDGE,"E5");var subQ1=sQuery(id+"F9.wireOp",EDGE,"E4");Q59=makeQuery(id+"F19.boolean.opBoolean","SPLIT",EDGE,{"disambiguationData":[TD([makeQuery(id+"F10.boolean.opBoolean","COPY",FACE,{"derivedFrom":makeQuery(id+"F10.opExtrude","SWEPT_FACE",FACE,{"disambiguationData":[OSD([subQ1])]})})])],"derivedFrom":makeQuery(id+"F13.boolean.opBoolean","COPY",EDGE,{"disambiguationData":[OD(0.0)],"derivedFrom":makeQuery(id+"F13.opExtrude","CAP_EDGE",EDGE,{"disambiguationData":[OSD([subQ0])],"isStart":false})})});}
            var Q60;
            {var subQ0=sQuery(id+"F6.wireOp",EDGE,"E3");var subQ1=sQuery(id+"F18.wireOp",EDGE,"E7");var subQ2=sQuery(id+"F3.wireOp",EDGE,"E2");Q60=makeQuery(id+"F19.boolean.opBoolean","COPY",EDGE,{"disambiguationData":[TD([makeQuery(id+"F4.boolean.opBoolean","COPY",FACE,{"derivedFrom":makeQuery(id+"F4.opExtrude","SWEPT_FACE",FACE,{"disambiguationData":[OSD([subQ2])]})}),makeQuery(id+"F4.boolean.opBoolean","COPY",FACE,{"derivedFrom":makeQuery(id+"F4.opExtrude","CAP_FACE",FACE,{"disambiguationData":[OSD([subQ2])],"isStart":false})}),makeQuery(id+"F7.boolean.opBoolean","COPY",FACE,{"derivedFrom":makeQuery(id+"F7.opExtrude","SWEPT_FACE",FACE,{"disambiguationData":[OSD([subQ0])]})}),makeQuery(id+"F7.boolean.opBoolean","COPY",FACE,{"derivedFrom":makeQuery(id+"F7.opExtrude","CAP_FACE",FACE,{"disambiguationData":[OSD([subQ0])],"isStart":false})}),makeQuery(id+"F19.opExtrude","SWEPT_FACE",FACE,{"disambiguationData":[OSD([subQ1])]}),makeQuery(id+"F19.opExtrude","CAP_FACE",FACE,{"disambiguationData":[OSD([subQ1])],"isStart":false})])],"derivedFrom":makeQuery(id+"F19.opExtrude","CAP_EDGE",EDGE,{"disambiguationData":[OSD([subQ1])],"isStart":false})});}
            var Q61;
            {var subQ0=sQuery(id+"F9.wireOp",EDGE,"E4");var subQ1=sQuery(id+"F18.wireOp",EDGE,"E7");var subQ2=sQuery(id+"F3.wireOp",EDGE,"E2");Q61=makeQuery(id+"F19.boolean.opBoolean","COPY",EDGE,{"disambiguationData":[TD([makeQuery(id+"F4.boolean.opBoolean","COPY",FACE,{"derivedFrom":makeQuery(id+"F4.opExtrude","SWEPT_FACE",FACE,{"disambiguationData":[OSD([subQ2])]})}),makeQuery(id+"F4.boolean.opBoolean","COPY",FACE,{"derivedFrom":makeQuery(id+"F4.opExtrude","CAP_FACE",FACE,{"disambiguationData":[OSD([subQ2])],"isStart":false})}),makeQuery(id+"F10.boolean.opBoolean","COPY",FACE,{"derivedFrom":makeQuery(id+"F10.opExtrude","SWEPT_FACE",FACE,{"disambiguationData":[OSD([subQ0])]})}),makeQuery(id+"F10.boolean.opBoolean","COPY",FACE,{"derivedFrom":makeQuery(id+"F10.opExtrude","CAP_FACE",FACE,{"disambiguationData":[OSD([subQ0])],"isStart":false})}),makeQuery(id+"F19.opExtrude","SWEPT_FACE",FACE,{"disambiguationData":[OSD([subQ1])]}),makeQuery(id+"F19.opExtrude","CAP_FACE",FACE,{"disambiguationData":[OSD([subQ1])],"isStart":false})])],"derivedFrom":makeQuery(id+"F19.opExtrude","CAP_EDGE",EDGE,{"disambiguationData":[OSD([subQ1])],"isStart":false})});}
            var Q62;
            {var subQ0=sQuery(id+"F12.wireOp",EDGE,"E5");var subQ1=sQuery(id+"F6.wireOp",EDGE,"E3");var subQ2=sQuery(id+"F18.wireOp",EDGE,"E7");Q62=makeQuery(id+"F19.boolean.opBoolean","COPY",EDGE,{"disambiguationData":[TD([makeQuery(id+"F7.boolean.opBoolean","COPY",FACE,{"derivedFrom":makeQuery(id+"F7.opExtrude","SWEPT_FACE",FACE,{"disambiguationData":[OSD([subQ1])]})}),makeQuery(id+"F7.boolean.opBoolean","COPY",FACE,{"derivedFrom":makeQuery(id+"F7.opExtrude","CAP_FACE",FACE,{"disambiguationData":[OSD([subQ1])],"isStart":false})}),makeQuery(id+"F13.boolean.opBoolean","COPY",FACE,{"derivedFrom":makeQuery(id+"F13.opExtrude","SWEPT_FACE",FACE,{"disambiguationData":[OSD([subQ0])]})}),makeQuery(id+"F13.boolean.opBoolean","COPY",FACE,{"derivedFrom":makeQuery(id+"F13.opExtrude","CAP_FACE",FACE,{"disambiguationData":[OSD([subQ0])],"isStart":false})}),makeQuery(id+"F19.opExtrude","SWEPT_FACE",FACE,{"disambiguationData":[OSD([subQ2])]}),makeQuery(id+"F19.opExtrude","CAP_FACE",FACE,{"disambiguationData":[OSD([subQ2])],"isStart":false})])],"derivedFrom":makeQuery(id+"F19.opExtrude","CAP_EDGE",EDGE,{"disambiguationData":[OSD([subQ2])],"isStart":false})});}
            var Q63;
            {var subQ0=sQuery(id+"F12.wireOp",EDGE,"E5");var subQ1=sQuery(id+"F9.wireOp",EDGE,"E4");var subQ2=sQuery(id+"F18.wireOp",EDGE,"E7");Q63=makeQuery(id+"F19.boolean.opBoolean","COPY",EDGE,{"disambiguationData":[TD([makeQuery(id+"F10.boolean.opBoolean","COPY",FACE,{"derivedFrom":makeQuery(id+"F10.opExtrude","SWEPT_FACE",FACE,{"disambiguationData":[OSD([subQ1])]})}),makeQuery(id+"F10.boolean.opBoolean","COPY",FACE,{"derivedFrom":makeQuery(id+"F10.opExtrude","CAP_FACE",FACE,{"disambiguationData":[OSD([subQ1])],"isStart":false})}),makeQuery(id+"F13.boolean.opBoolean","COPY",FACE,{"derivedFrom":makeQuery(id+"F13.opExtrude","SWEPT_FACE",FACE,{"disambiguationData":[OSD([subQ0])]})}),makeQuery(id+"F13.boolean.opBoolean","COPY",FACE,{"derivedFrom":makeQuery(id+"F13.opExtrude","CAP_FACE",FACE,{"disambiguationData":[OSD([subQ0])],"isStart":false})}),makeQuery(id+"F19.opExtrude","SWEPT_FACE",FACE,{"disambiguationData":[OSD([subQ2])]}),makeQuery(id+"F19.opExtrude","CAP_FACE",FACE,{"disambiguationData":[OSD([subQ2])],"isStart":false})])],"derivedFrom":makeQuery(id+"F19.opExtrude","CAP_EDGE",EDGE,{"disambiguationData":[OSD([subQ2])],"isStart":false})});}
            var Q64;
            Q64=makeQuery(id+"F19.boolean.opBoolean","INTERSECT",EDGE,{"derivedFrom":[makeQuery(id+"F1.opRevolve","SWEPT_FACE",FACE,{"disambiguationData":[OSD([sQuery(id+"F0.wireOp",EDGE,"E0")])]}),makeQuery(id+"F19.opExtrude","SWEPT_FACE",FACE,{"disambiguationData":[OSD([sQuery(id+"F18.wireOp",EDGE,"E7")])]})]});
            var Q65;
            Q65=makeQuery(id+"F19.boolean.opBoolean","INTERSECT",EDGE,{"derivedFrom":[makeQuery(id+"F4.boolean.opBoolean","COPY",FACE,{"derivedFrom":makeQuery(id+"F4.opExtrude","CAP_FACE",FACE,{"disambiguationData":[OSD([sQuery(id+"F3.wireOp",EDGE,"E2")])],"isStart":false})}),makeQuery(id+"F19.opExtrude","CAP_FACE",FACE,{"disambiguationData":[OSD([sQuery(id+"F18.wireOp",EDGE,"E7")])],"isStart":false})]});
            var Q66;
            Q66=makeQuery(id+"F19.boolean.opBoolean","INTERSECT",EDGE,{"derivedFrom":[makeQuery(id+"F7.boolean.opBoolean","COPY",FACE,{"derivedFrom":makeQuery(id+"F7.opExtrude","CAP_FACE",FACE,{"disambiguationData":[OSD([sQuery(id+"F6.wireOp",EDGE,"E3")])],"isStart":false})}),makeQuery(id+"F19.opExtrude","CAP_FACE",FACE,{"disambiguationData":[OSD([sQuery(id+"F18.wireOp",EDGE,"E7")])],"isStart":false})]});
            fillet(context, id + "F20", {"entities" : qUnion([Q0, Q1, Q2, Q3, Q4, Q5, Q6, Q7, Q8, Q9, Q10, Q11, Q12, Q13, Q14, Q15, Q16, Q17, Q18, Q19, Q20, Q21, Q22, Q23, Q24, Q25, Q26, Q27, Q28, Q29, Q30, Q31, Q32, Q33, Q34, Q35, Q36, Q37, Q38, Q39, Q40, Q41, Q42, Q43, Q44, Q45, Q46, Q47, Q48, Q49, Q50, Q51, Q52, Q53, Q54, Q55, Q56, Q57, Q58, Q59, Q60, Q61, Q62, Q63, Q64, Q65, Q66]), "radius" : 0.5 * mm, "tangentPropagation" : true, "allowEdgeOverflow" : false});
        }
    });
